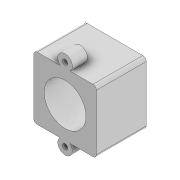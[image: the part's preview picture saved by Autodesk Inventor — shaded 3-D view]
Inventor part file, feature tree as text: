
AUTODESK INVENTOR PART (.ipt)
format: ipt  version: 2022 (Build 260153000, 153)  size: 134,656 bytes
history: native  units: mm
features: extrude x2, sketch x2, fillet x1, projected_geometry x1
ambient origin geometry x8: Origin, YZ Plane, XZ Plane, XY Plane, X Axis, Y Axis, Z Axis, Center Point
bodies: Volumenkörper1 (feature_tree)
feature tree (6):
  extrude  "Extrusion1"  Depth=18.0mm
  fillet  "Rundung1"  Radius=12.0mm
  extrude  "Extrusion2"  Depth=1.0mm
  sketch  "Skizze1"  dims[d0=18.0mm d1=18.0mm d2=12.0mm]
  sketch  "Skizze2"  dims[d3=10.0mm d4=0.0mm d5=1.0mm d6=1.5mm d7=1.5mm d8=10.5mm d9=10.5mm d10=4.2mm d11=4.2mm d12=4.3mm d13=0.0mm]
  projected_geometry  "Projizierte Kontur1"
